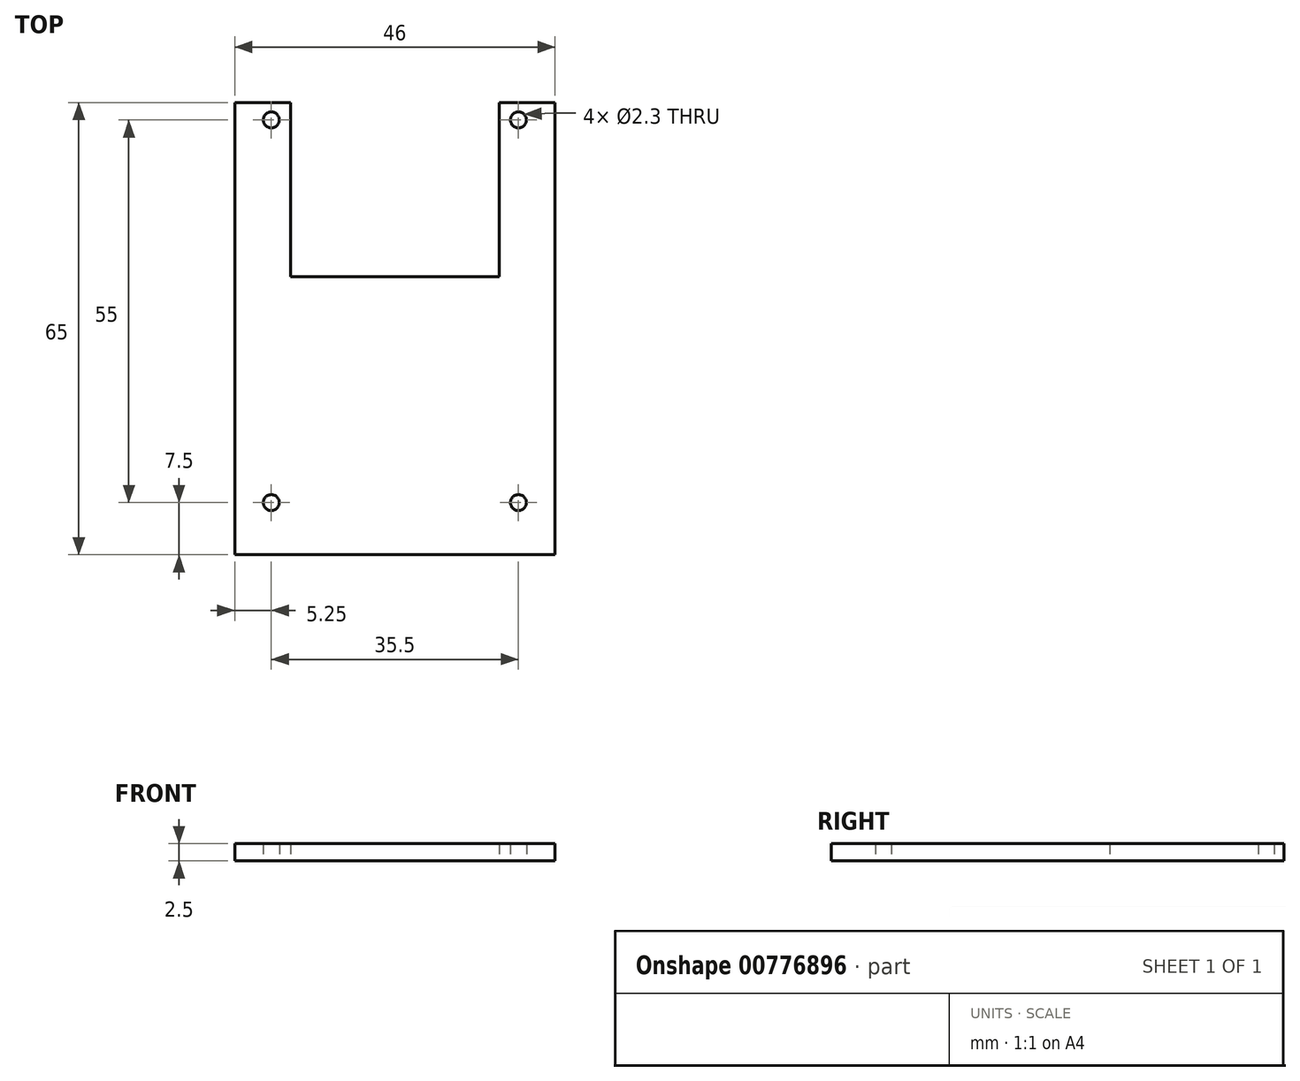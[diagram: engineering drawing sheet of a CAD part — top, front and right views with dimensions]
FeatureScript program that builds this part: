
annotation { "Feature Type Name" : "Feature", "Feature Type Description" : "" }
export const myFeature = defineFeature(function(context is Context, id is Id, definition is map)
    precondition{}
    {
        {
            var Q0;
            Q0=qCreatedBy(makeId("Top.planeOp"),FACE);
            var sketch = newSketch(context, id + "F0", { "sketchPlane" : qUnion([Q0])});
            skLineSegment(sketch, "E0.bottom", {"start": v(23, -32.5) * mm, "end": v(-23, -32.5) * mm});
            skLineSegment(sketch, "E0.top", {"start": v(23, 32.5) * mm, "end": v(-23, 32.5) * mm});
            skLineSegment(sketch, "E0.left", {"start": v(23, -32.5) * mm, "end": v(23, 32.5) * mm});
            skLineSegment(sketch, "E0.right", {"start": v(-23, -32.5) * mm, "end": v(-23, 32.5) * mm});
            skPoint(sketch, "E0.middle", {"position": v(0, 0) * mm});
            skCircle(sketch, "E1", {"center": v(-17.75, 30) * mm, "radius": 1.15 * mm});
            skCircle(sketch, "E2", {"center": v(-17.75, -25) * mm, "radius": 1.15 * mm});
            skCircle(sketch, "E3.MirrorC", {"center": v(17.75, 30) * mm, "radius": 1.15 * mm});
            skCircle(sketch, "E4.MirrorC", {"center": v(17.75, -25) * mm, "radius": 1.15 * mm});
            skLineSegment(sketch, "E5", {"start": v(-17.75, 32.5) * mm, "end": v(-17.75, -32.5) * mm, "construction": true});
            skLineSegment(sketch, "E6.bottom", {"start": v(-15, 32.5) * mm, "end": v(15, 32.5) * mm});
            skLineSegment(sketch, "E6.top", {"start": v(-15, 7.5) * mm, "end": v(15, 7.5) * mm});
            skLineSegment(sketch, "E6.left", {"start": v(-15, 32.5) * mm, "end": v(-15, 7.5) * mm});
            skLineSegment(sketch, "E6.right", {"start": v(15, 32.5) * mm, "end": v(15, 7.5) * mm});
            skLineSegment(sketch, "E7", {"start": v(0, 0) * mm, "end": v(0, 32.5) * mm, "construction": true});
            skSolve(sketch);
        }
        {
            var Q0;
            Q0=makeQuery(id+"F0.imprint","IMPRINT",FACE,{"disambiguationData":[TD([[makeQuery(id+"F0.imprint","IMPRINT",EDGE,{"derivedFrom":sQuery(id+"F0.wireOp",EDGE,"E0.bottom")}),-1.0]])]});
            extrude(context, id + "F1", {"entities" : qUnion([Q0]), "depth" : 2.5 * mm, "offsetDistance" : 25 * mm});
        }
    });
